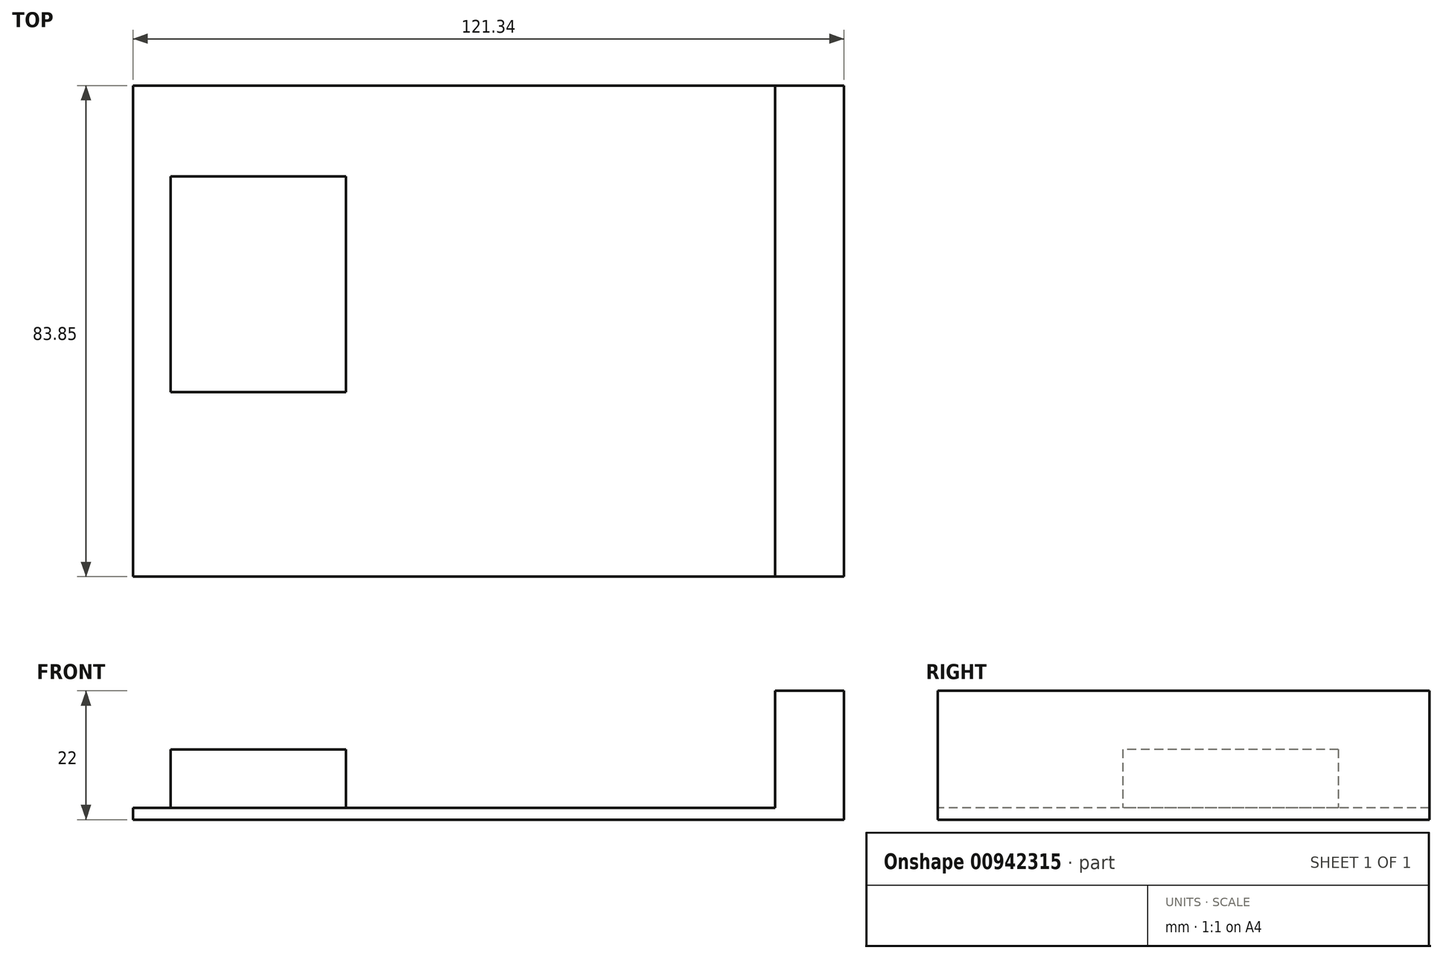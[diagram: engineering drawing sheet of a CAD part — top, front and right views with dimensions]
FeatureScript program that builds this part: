
annotation { "Feature Type Name" : "Feature", "Feature Type Description" : "" }
export const myFeature = defineFeature(function(context is Context, id is Id, definition is map)
    precondition{}
    {
        {
            var Q0;
            Q0=qCreatedBy(makeId("Top.planeOp"),FACE);
            var sketch = newSketch(context, id + "F0", { "sketchPlane" : qUnion([Q0])});
            skLineSegment(sketch, "E0.bottom", {"start": v(-57.34, 40.48) * mm, "end": v(64, 40.48) * mm});
            skLineSegment(sketch, "E0.top", {"start": v(-57.34, -43.37) * mm, "end": v(64, -43.37) * mm});
            skLineSegment(sketch, "E0.left", {"start": v(-57.34, 40.48) * mm, "end": v(-57.34, -43.37) * mm});
            skLineSegment(sketch, "E0.right", {"start": v(64, 40.48) * mm, "end": v(64, -43.37) * mm});
            skLineSegment(sketch, "E1.bottom", {"start": v(-50.91, 24.96) * mm, "end": v(-20.96, 24.96) * mm});
            skLineSegment(sketch, "E1.top", {"start": v(-50.91, -11.87) * mm, "end": v(-20.96, -11.87) * mm});
            skLineSegment(sketch, "E1.left", {"start": v(-50.91, 24.96) * mm, "end": v(-50.91, -11.87) * mm});
            skLineSegment(sketch, "E1.right", {"start": v(-20.96, 24.96) * mm, "end": v(-20.96, -11.87) * mm});
            skLineSegment(sketch, "E2.bottom", {"start": v(64, 40.48) * mm, "end": v(64, 40.48) * mm});
            skLineSegment(sketch, "E2.top", {"start": v(64, -43.37) * mm, "end": v(64, -43.37) * mm});
            skLineSegment(sketch, "E3.bottom", {"start": v(64, 40.48) * mm, "end": v(52.24, 40.48) * mm});
            skLineSegment(sketch, "E3.top", {"start": v(64, -43.37) * mm, "end": v(52.24, -43.37) * mm});
            skLineSegment(sketch, "E3.right", {"start": v(52.24, 40.48) * mm, "end": v(52.24, -43.37) * mm});
            skSolve(sketch);
        }
        {
            var Q0;
            {var subQ0=sQuery(id+"F0.wireOp",EDGE,"E0.left");var subQ7=sQuery(id+"F0.wireOp",EDGE,"E0.right");Q0=qUnion([makeQuery(id+"F0.imprint","IMPRINT",FACE,{"disambiguationData":[TD([[makeQuery(id+"F0.imprint","IMPRINT",EDGE,{"derivedFrom":subQ7}),-1.0]])]}),makeQuery(id+"F0.imprint","IMPRINT",FACE,{"disambiguationData":[TD([[makeQuery(id+"F0.imprint","IMPRINT",EDGE,{"derivedFrom":subQ0}),1.0]])]})]);}
            var Q1;
            Q1=makeQuery(id+"F0.imprint","IMPRINT",FACE,{"disambiguationData":[TD([[makeQuery(id+"F0.imprint","IMPRINT",EDGE,{"derivedFrom":sQuery(id+"F0.wireOp",EDGE,"E1.bottom")}),-1.0]])]});
            extrude(context, id + "F1", {"entities" : qUnion([Q0, Q1]), "oppositeDirection" : true, "depth" : 2 * mm, "offsetDistance" : 25 * mm});
        }
        {
            var Q0;
            Q0=makeQuery(id+"F0.imprint","IMPRINT",FACE,{"disambiguationData":[TD([[makeQuery(id+"F0.imprint","IMPRINT",EDGE,{"derivedFrom":sQuery(id+"F0.wireOp",EDGE,"E1.bottom")}),-1.0]])]});
            extrude(context, id + "F2", {"entities" : qUnion([Q0]), "operationType" : NewBodyOperationType.ADD, "depth" : 10 * mm, "offsetDistance" : 25 * mm});
        }
        {
            var Q0;
            {var subQ0=sQuery(id+"F0.wireOp",EDGE,"E0.right");Q0=makeQuery(id+"F0.imprint","IMPRINT",FACE,{"disambiguationData":[TD([[makeQuery(id+"F0.imprint","IMPRINT",EDGE,{"derivedFrom":subQ0}),-1.0]])]});}
            extrude(context, id + "F3", {"entities" : qUnion([Q0]), "operationType" : NewBodyOperationType.ADD, "depth" : 20 * mm, "offsetDistance" : 25 * mm});
        }
    });
